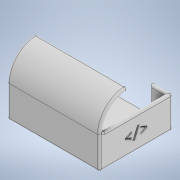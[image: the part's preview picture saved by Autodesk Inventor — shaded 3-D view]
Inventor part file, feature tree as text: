
AUTODESK INVENTOR PART (.ipt)
format: ipt  version: 2020 (Build 240168000, 168)  size: 252,928 bytes
history: native  units: in
note: dims shown in document units (in); Inventor stores cm internally (conversion verified against a paired STEP export)
features: sketch x5, extrude x4, fillet x2, emboss x1
ambient origin geometry x8: Origin, YZ Plane, XZ Plane, XY Plane, X Axis, Y Axis, Z Axis, Center Point
bodies: Solid1 (feature_tree)
feature tree (12):
  extrude  "Extrusion1"  Depth=1.378in
  extrude  "Extrusion2"  Depth=0.0787in
  extrude  "Extrusion3"  Depth=0.0787in
  extrude  "Extrusion4"  Depth=0.0787in
  fillet  "Fillet1"  Radius=0.0787in
  fillet  "Fillet2"  Radius=0.0787in
  emboss  "Emboss1"
  sketch  "Sketch1"  dims[d0=1.7717in d1=1.378in]
  sketch  "Sketch2"  dims[d2=0.0787in d3=0.0787in]
  sketch  "Sketch3"  dims[d4=0.0787in d5=0.0787in]
  sketch  "Sketch4"  dims[d6=0.0787in d7=0.0in d8=0.0787in d9=0.0787in d10=0.0787in]
  sketch  "Sketch5"  dims[d11=0.0787in d12=0.3937in d13=0.5906in d14=0.0in d15=0.5906in d16=0.5906in d17=0.0in d18=1.9685in d19=0.0in d20=0.0787in d21=0.0394in d22=0.0787in d23=0.0in]
